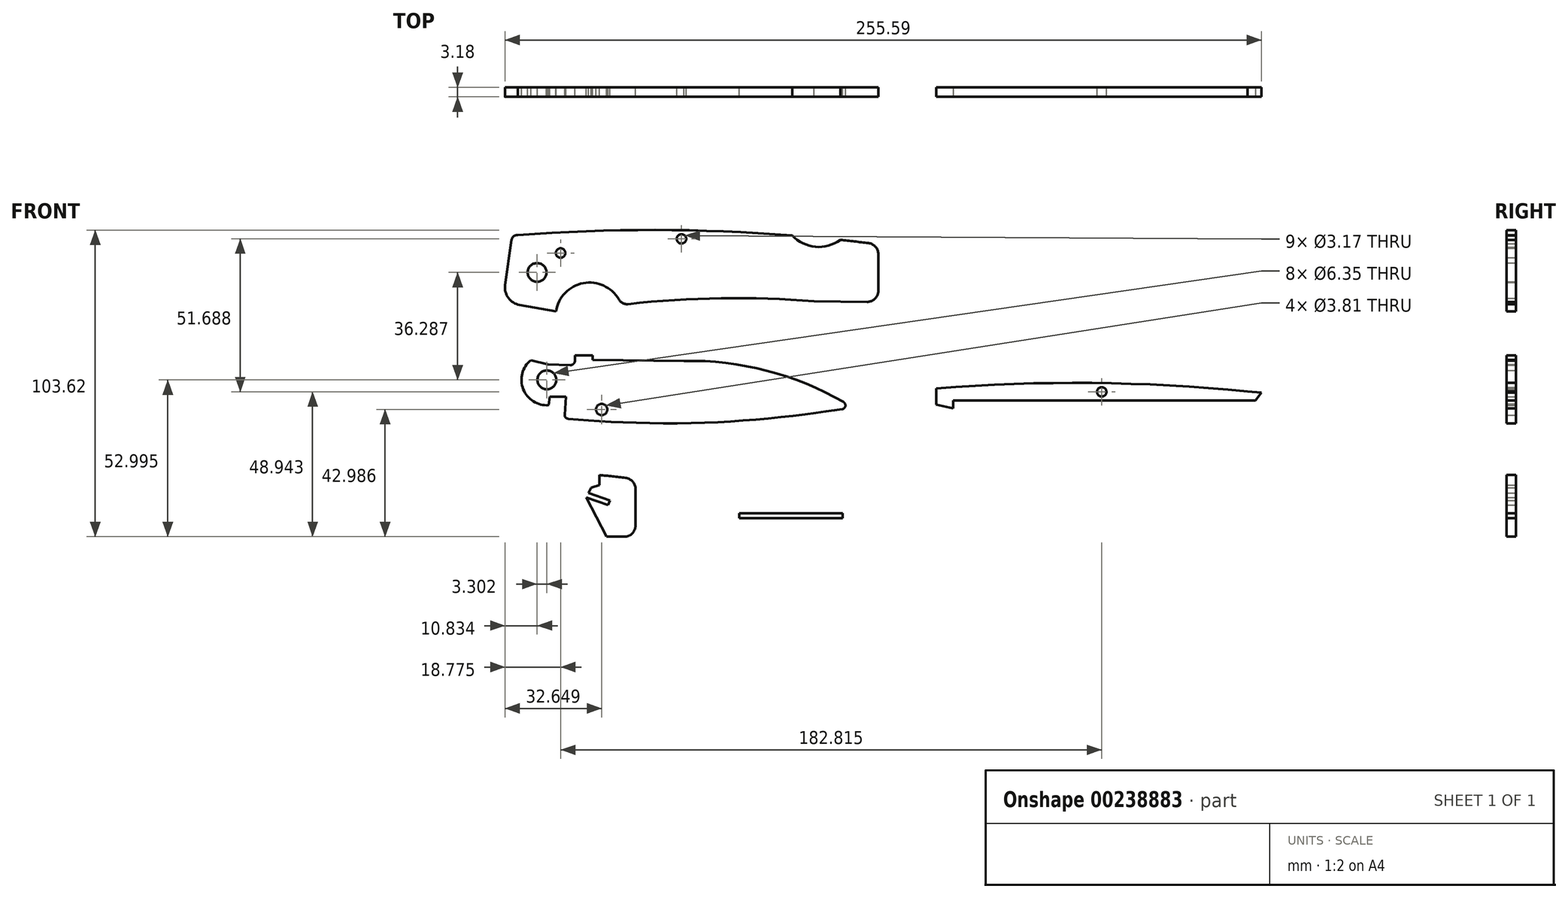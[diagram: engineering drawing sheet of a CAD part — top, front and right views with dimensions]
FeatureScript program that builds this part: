
annotation { "Feature Type Name" : "Feature", "Feature Type Description" : "" }
export const myFeature = defineFeature(function(context is Context, id is Id, definition is map)
    precondition{}
    {
        {
            var Q0;
            Q0=qCreatedBy(makeId("Front.planeOp"),FACE);
            var sketch = newSketch(context, id + "F0", { "sketchPlane" : qUnion([Q0])});
            skLineSegment(sketch, "E0", {"start": v(-111.57, 31.31) * mm, "end": v(-113.73, 16.08) * mm});
            skLineSegment(sketch, "E1", {"start": v(-96.53, 7.19) * mm, "end": v(-108.84, 9.35) * mm});
            skArc(sketch, "E2", {"start": v(-113.73, 16.08) * mm, "mid": v(-112.65, 11.72) * mm, "end": v(-108.84, 9.35) * mm});
            skPoint(sketch, "E2.first.point", {"position": v(-113.73, 16.08) * mm});
            skPoint(sketch, "E2.second.point", {"position": v(-112.97, 12.22) * mm});
            skPoint(sketch, "E2.third.point", {"position": v(-108.84, 9.35) * mm});
            skArc(sketch, "E3", {"start": v(-16.77, 32.83) * mm, "mid": v(-63.45, 34.67) * mm, "end": v(-110.13, 32.9) * mm});
            skPoint(sketch, "E3.first.point", {"position": v(-110.13, 32.9) * mm});
            skPoint(sketch, "E3.second.point", {"position": v(-61.22, 34.67) * mm});
            skPoint(sketch, "E3.third.point", {"position": v(-16.83, 32.83) * mm});
            skArc(sketch, "E4", {"start": v(-16.77, 32.83) * mm, "mid": v(-8.91, 29) * mm, "end": v(-0.5, 31.33) * mm});
            skPoint(sketch, "E4.first.point", {"position": v(-16.77, 32.83) * mm});
            skPoint(sketch, "E4.second.point", {"position": v(-7.82, 28.95) * mm});
            skPoint(sketch, "E4.third.point", {"position": v(-0.5, 31.33) * mm});
            skArc(sketch, "E5", {"start": v(-75.32, 11.2) * mm, "mid": v(-87.35, 16.73) * mm, "end": v(-96.53, 7.19) * mm});
            skArc(sketch, "E6", {"start": v(-9.33, 10.62) * mm, "mid": v(-40.8, 11.64) * mm, "end": v(-72.23, 9.64) * mm});
            skArc(sketch, "E7", {"start": v(-75.32, 11.2) * mm, "mid": v(-74.01, 9.96) * mm, "end": v(-72.23, 9.64) * mm});
            skPoint(sketch, "E7.first.point", {"position": v(-75.32, 11.2) * mm});
            skPoint(sketch, "E7.second.point", {"position": v(-73.68, 9.81) * mm});
            skPoint(sketch, "E7.third.point", {"position": v(-72.23, 9.64) * mm});
            skArc(sketch, "E8.trimOffspring", {"start": v(-75.32, 11.2) * mm, "mid": v(-80.66, 15.97) * mm, "end": v(-87.78, 16.64) * mm});
            skCircle(sketch, "E9", {"center": v(-102.96, 20.33) * mm, "radius": 3.18 * mm});
            skCircle(sketch, "E10", {"center": v(-95.01, 26.9) * mm, "radius": 1.59 * mm});
            skCircle(sketch, "E11", {"center": v(-54.16, 31.68) * mm, "radius": 1.59 * mm});
            skLineSegment(sketch, "E12", {"start": v(12.33, 26.47) * mm, "end": v(12.33, 14.2) * mm});
            skLineSegment(sketch, "E13", {"start": v(8.47, 10.39) * mm, "end": v(-9.33, 10.62) * mm});
            skArc(sketch, "E14", {"start": v(8.47, 10.39) * mm, "mid": v(11.2, 11.49) * mm, "end": v(12.33, 14.2) * mm});
            skArc(sketch, "E15.trimOffspring", {"start": v(8.98, 30.25) * mm, "mid": v(4.24, 30.81) * mm, "end": v(-0.5, 31.33) * mm});
            skArc(sketch, "E16", {"start": v(12.33, 26.47) * mm, "mid": v(11.37, 29) * mm, "end": v(8.98, 30.25) * mm});
            skPoint(sketch, "E17.orphan", {"position": v(12.33, 29.84) * mm});
            skLineSegment(sketch, "E18", {"start": v(31.9, -24.28) * mm, "end": v(31.9, -18.8) * mm});
            skLineSegment(sketch, "E19", {"start": v(31.9, -24.28) * mm, "end": v(37.6, -25.76) * mm});
            skLineSegment(sketch, "E20", {"start": v(37.6, -25.76) * mm, "end": v(37.6, -22.95) * mm});
            skLineSegment(sketch, "E21", {"start": v(37.6, -22.95) * mm, "end": v(137.02, -22.95) * mm});
            skLineSegment(sketch, "E22", {"start": v(137.02, -22.95) * mm, "end": v(139.23, -20.03) * mm});
            skArc(sketch, "E23", {"start": v(139.23, -20.03) * mm, "mid": v(85.6, -17.02) * mm, "end": v(31.9, -18.8) * mm});
            skLineSegment(sketch, "E24.bottom", {"start": v(-34.72, -61.08) * mm, "end": v(0.2, -61.08) * mm});
            skLineSegment(sketch, "E24.top", {"start": v(-34.72, -62.73) * mm, "end": v(0.2, -62.73) * mm});
            skLineSegment(sketch, "E24.left", {"start": v(-34.72, -61.08) * mm, "end": v(-34.72, -62.73) * mm});
            skLineSegment(sketch, "E24.right", {"start": v(0.2, -61.08) * mm, "end": v(0.2, -62.73) * mm});
            skLineSegment(sketch, "E25", {"start": v(-86.33, -55.63) * mm, "end": v(-79.54, -68.88) * mm});
            skLineSegment(sketch, "E26", {"start": v(-82.53, -48) * mm, "end": v(-85.53, -54.13) * mm});
            skLineSegment(sketch, "E27", {"start": v(-85.53, -54.13) * mm, "end": v(-78.39, -56.71) * mm});
            skLineSegment(sketch, "E28", {"start": v(-78.39, -56.71) * mm, "end": v(-78.96, -58.29) * mm});
            skLineSegment(sketch, "E29", {"start": v(-78.96, -58.29) * mm, "end": v(-86.33, -55.63) * mm});
            skLineSegment(sketch, "E30", {"start": v(-69.7, -52.87) * mm, "end": v(-69.7, -65.14) * mm});
            skLineSegment(sketch, "E31", {"start": v(-73.56, -68.95) * mm, "end": v(-79.54, -68.88) * mm});
            skArc(sketch, "E32", {"start": v(-73.56, -68.95) * mm, "mid": v(-70.84, -67.85) * mm, "end": v(-69.7, -65.14) * mm});
            skArc(sketch, "E33.trimOffspring", {"start": v(-73.05, -49.09) * mm, "mid": v(-77.79, -48.53) * mm, "end": v(-82.53, -48) * mm});
            skArc(sketch, "E34", {"start": v(-69.7, -52.87) * mm, "mid": v(-70.66, -50.34) * mm, "end": v(-73.05, -49.09) * mm});
            skPoint(sketch, "E35.orphan", {"position": v(-69.7, -49.5) * mm});
            skCircle(sketch, "E36", {"center": v(-99.65, -15.96) * mm, "radius": 3.18 * mm});
            skCircle(sketch, "E37", {"center": v(-81.14, -25.96) * mm, "radius": 1.9 * mm});
            skLineSegment(sketch, "E38", {"start": v(-90.15, -7.62) * mm, "end": v(-84.13, -7.62) * mm});
            skLineSegment(sketch, "E39", {"start": v(-84.13, -7.62) * mm, "end": v(-84.13, -9.15) * mm});
            skLineSegment(sketch, "E40", {"start": v(-105.04, -9.29) * mm, "end": v(-99.25, -10.7) * mm});
            skLineSegment(sketch, "E41", {"start": v(-99.25, -10.7) * mm, "end": v(-91.8, -10.98) * mm});
            skLineSegment(sketch, "E42", {"start": v(-90.15, -7.62) * mm, "end": v(-90.15, -9.4) * mm});
            skArc(sketch, "E43", {"start": v(-91.8, -10.98) * mm, "mid": v(-90.63, -10.54) * mm, "end": v(-90.15, -9.4) * mm});
            skArc(sketch, "E44", {"start": v(-105.04, -9.29) * mm, "mid": v(-107.63, -19.1) * mm, "end": v(-99.02, -24.5) * mm});
            skLineSegment(sketch, "E45", {"start": v(-99.02, -24.5) * mm, "end": v(-98.73, -21.6) * mm});
            skLineSegment(sketch, "E46", {"start": v(-98.73, -21.6) * mm, "end": v(-93.2, -21.6) * mm});
            skLineSegment(sketch, "E47", {"start": v(-93.2, -21.6) * mm, "end": v(-93.73, -29) * mm});
            skLineSegment(sketch, "E48", {"start": v(-84.13, -9.15) * mm, "end": v(-53.31, -9.53) * mm});
            skArc(sketch, "E49", {"start": v(3.64, -25.31) * mm, "mid": v(-23.7, -13.3) * mm, "end": v(-53.31, -9.53) * mm});
            skFitSpline(sketch, "E50", {"points": [v(-93.73, -29) * mm, v(-76.51, -30.18) * mm, v(-49.65, -30.52) * mm, v(-25.17, -29) * mm, v(-5.36, -26.65) * mm, v(3.64, -25.31) * mm], "startDerivative": vector(84.42, -6.94) * mm, "endDerivative": vector(58.31, 8.48) * mm});
            skArc(sketch, "E51.trimOffspring", {"start": v(3.64, -25.31) * mm, "mid": v(-8.22, -18.94) * mm, "end": v(-20.8, -14.15) * mm});
            skArc(sketch, "E52", {"start": v(-109.52, 32.95) * mm, "mid": v(-110.87, 32.54) * mm, "end": v(-111.57, 31.31) * mm});
            skCircle(sketch, "E53", {"center": v(87.8, -20) * mm, "radius": 1.59 * mm});
            skPoint(sketch, "E54", {"position": v(87.9, -19.96) * mm});
            skSolve(sketch);
        }
        {
            var Q0;
            Q0=qSketchRegion(id+"F0",true);
            extrude(context, id + "F1", {"entities" : qUnion([Q0]), "depth" : 3.17 * mm});
        }
        {
            var Q0;
            Q0=makeQuery(id+"F1.opExtrude","CAP_FACE",FACE,{"disambiguationData":[OSD([sQuery(id+"F0.wireOp",EDGE,"E18"),sQuery(id+"F0.wireOp",EDGE,"E19"),sQuery(id+"F0.wireOp",EDGE,"E20"),sQuery(id+"F0.wireOp",EDGE,"E21"),sQuery(id+"F0.wireOp",EDGE,"E22"),sQuery(id+"F0.wireOp",EDGE,"E23"),sQuery(id+"F0.wireOp",EDGE,"E53")])],"isStart":false});
            var sketch = newSketch(context, id + "F2", { "sketchPlane" : qUnion([Q0])});
            skLineSegment(sketch, "E55", {"start": v(31.9, -24.28) * mm, "end": v(37.6, -25.63) * mm});
            skLineSegment(sketch, "E56", {"start": v(37.6, -25.63) * mm, "end": v(37.6, -25.76) * mm});
            skLineSegment(sketch, "E57", {"start": v(37.6, -25.76) * mm, "end": v(31.9, -24.28) * mm});
            skSolve(sketch);
        }
        {
            var Q0;
            Q0=qSketchRegion(id+"F2",true);
            extrude(context, id + "F3", {"entities" : qUnion([Q0]), "operationType" : NewBodyOperationType.REMOVE, "oppositeDirection" : true, "depth" : 25.4 * mm});
        }
        {
            var Q0;
            Q0=makeQuery(id+"F1.opExtrude","CAP_FACE",FACE,{"disambiguationData":[OSD([sQuery(id+"F0.wireOp",EDGE,"E18"),sQuery(id+"F0.wireOp",EDGE,"E19"),sQuery(id+"F0.wireOp",EDGE,"E20"),sQuery(id+"F0.wireOp",EDGE,"E21"),sQuery(id+"F0.wireOp",EDGE,"E22"),sQuery(id+"F0.wireOp",EDGE,"E23"),sQuery(id+"F0.wireOp",EDGE,"E53")])],"isStart":false});
            var sketch = newSketch(context, id + "F4", { "sketchPlane" : qUnion([Q0])});
            skLineSegment(sketch, "E58", {"start": v(134.64, -22.95) * mm, "end": v(139.72, -22.95) * mm});
            skLineSegment(sketch, "E59", {"start": v(139.72, -22.95) * mm, "end": v(141.8, -20.21) * mm});
            skLineSegment(sketch, "E60", {"start": v(141.8, -20.21) * mm, "end": v(137.02, -19.81) * mm});
            skLineSegment(sketch, "E61", {"start": v(137.02, -19.81) * mm, "end": v(134.64, -22.95) * mm});
            skSolve(sketch);
        }
        {
            var Q0;
            Q0=qSketchRegion(id+"F4",true);
            extrude(context, id + "F5", {"entities" : qUnion([Q0]), "operationType" : NewBodyOperationType.ADD, "oppositeDirection" : true, "depth" : 3.17 * mm});
        }
        {
            var Q0;
            Q0=makeQuery(id+"F1.opExtrude","CAP_FACE",FACE,{"disambiguationData":[OSD([sQuery(id+"F0.wireOp",EDGE,"E25"),sQuery(id+"F0.wireOp",EDGE,"E26"),sQuery(id+"F0.wireOp",EDGE,"E27"),sQuery(id+"F0.wireOp",EDGE,"E28"),sQuery(id+"F0.wireOp",EDGE,"E29"),sQuery(id+"F0.wireOp",EDGE,"E30"),sQuery(id+"F0.wireOp",EDGE,"E31"),sQuery(id+"F0.wireOp",EDGE,"E32"),sQuery(id+"F0.wireOp",EDGE,"E33.trimOffspring"),sQuery(id+"F0.wireOp",EDGE,"E34")])],"isStart":true});
            var sketch = newSketch(context, id + "F6", { "sketchPlane" : qUnion([Q0])});
            skLineSegment(sketch, "E62", {"start": v(81.85, -48.08) * mm, "end": v(81.85, -51.44) * mm});
            skLineSegment(sketch, "E63", {"start": v(81.85, -51.44) * mm, "end": v(84.69, -52.41) * mm});
            skLineSegment(sketch, "E64", {"start": v(84.69, -52.41) * mm, "end": v(82.53, -48) * mm});
            skLineSegment(sketch, "E65", {"start": v(82.53, -48) * mm, "end": v(81.85, -48.08) * mm});
            skSolve(sketch);
        }
        {
            var Q0;
            Q0=qSketchRegion(id+"F6",true);
            extrude(context, id + "F7", {"entities" : qUnion([Q0]), "operationType" : NewBodyOperationType.REMOVE, "oppositeDirection" : true, "depth" : 25.4 * mm});
        }
        {
            var Q0;
            Q0=makeQuery(id+"F1.opExtrude","SWEPT_EDGE",EDGE,{"disambiguationData":[OSD([sQuery(id+"F0.wireOp",EDGE,"E50"),sQuery(id+"F0.wireOp",EDGE,"E51.trimOffspring")])]});
            fillet(context, id + "F8", {"entities" : qUnion([Q0]), "radius" : 1.27 * mm, "tangentPropagation" : true, "allowEdgeOverflow" : false});
        }
    });
